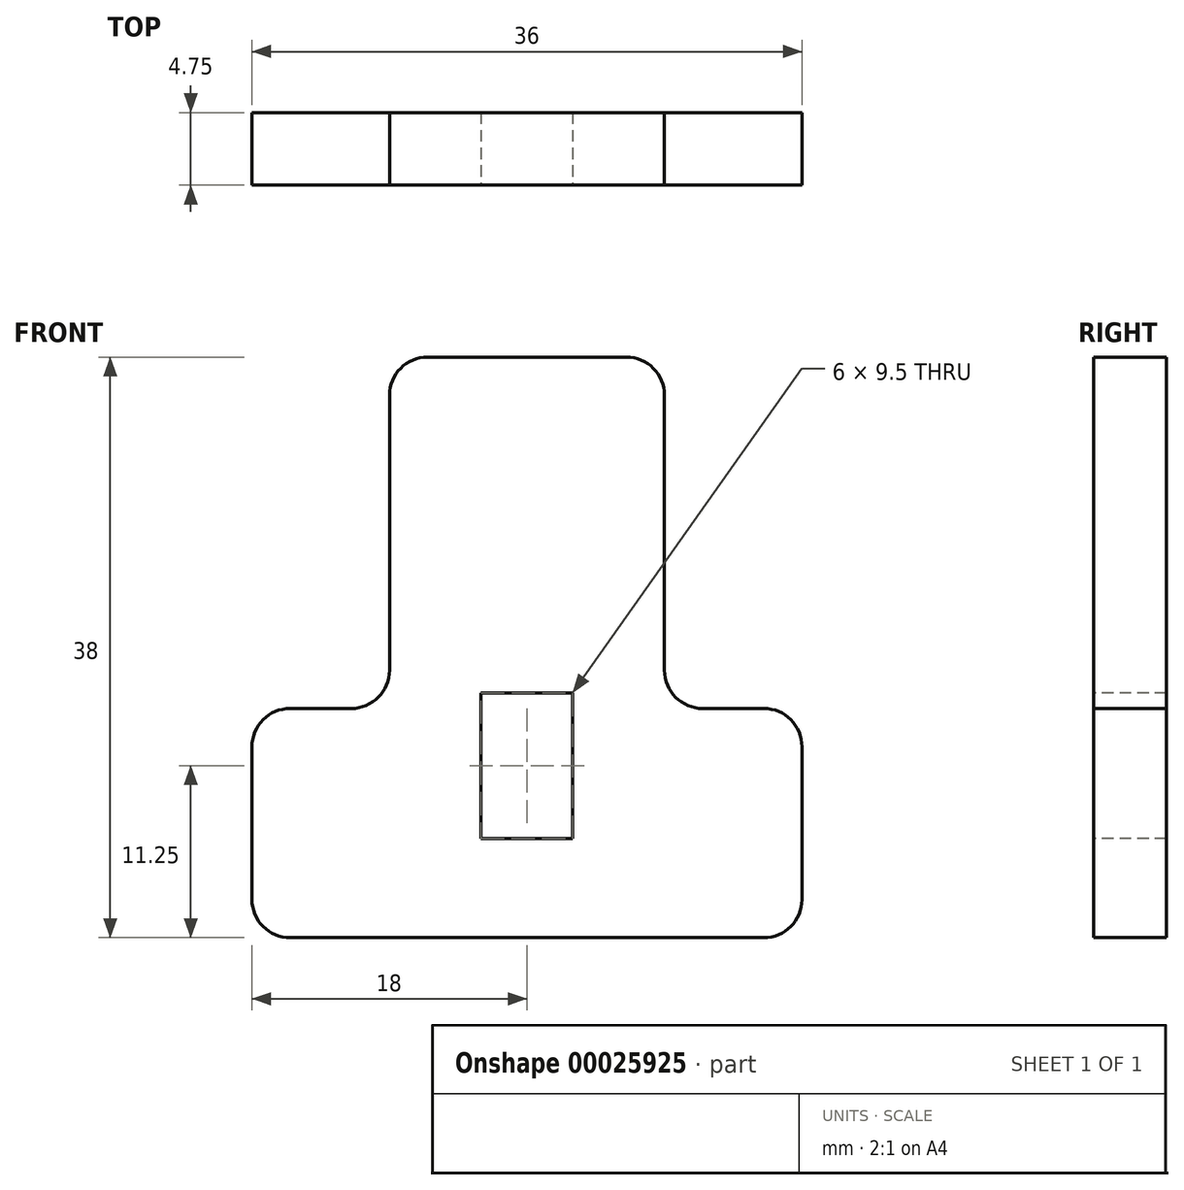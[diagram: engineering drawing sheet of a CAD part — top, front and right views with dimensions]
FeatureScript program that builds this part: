
annotation { "Feature Type Name" : "Feature", "Feature Type Description" : "" }
export const myFeature = defineFeature(function(context is Context, id is Id, definition is map)
    precondition{}
    {
        {
            var Q0;
            Q0=qCreatedBy(makeId("Front.planeOp"),FACE);
            var sketch = newSketch(context, id + "F0", { "sketchPlane" : qUnion([Q0])});
            skLineSegment(sketch, "E0", {"start": v(0, -15) * mm, "end": v(-18, -15) * mm});
            skLineSegment(sketch, "E1", {"start": v(-18, -15) * mm, "end": v(-18, 0) * mm});
            skLineSegment(sketch, "E2", {"start": v(-18, 0) * mm, "end": v(-9, 0) * mm});
            skLineSegment(sketch, "E3", {"start": v(-9, 0) * mm, "end": v(-9, 23) * mm});
            skLineSegment(sketch, "E4", {"start": v(-9, 23) * mm, "end": v(0, 23) * mm});
            skLineSegment(sketch, "E5.MirrorCS", {"start": v(9, 23) * mm, "end": v(0, 23) * mm});
            skLineSegment(sketch, "E6.MirrorCS", {"start": v(9, 0) * mm, "end": v(9, 23) * mm});
            skLineSegment(sketch, "E7.MirrorCS", {"start": v(18, 0) * mm, "end": v(9, 0) * mm});
            skLineSegment(sketch, "E8.MirrorCS", {"start": v(18, -15) * mm, "end": v(18, 0) * mm});
            skLineSegment(sketch, "E9.MirrorCS", {"start": v(0, -15) * mm, "end": v(18, -15) * mm});
            skLineSegment(sketch, "E10", {"start": v(0, 1) * mm, "end": v(-3, 1) * mm});
            skLineSegment(sketch, "E11", {"start": v(-3, 1) * mm, "end": v(-3, -8.5) * mm});
            skLineSegment(sketch, "E12", {"start": v(-3, -8.5) * mm, "end": v(0, -8.5) * mm});
            skLineSegment(sketch, "E13.MirrorCS", {"start": v(0, 1) * mm, "end": v(3, 1) * mm});
            skLineSegment(sketch, "E14.MirrorCS", {"start": v(3, 1) * mm, "end": v(3, -8.5) * mm});
            skLineSegment(sketch, "E15.MirrorCS", {"start": v(3, -8.5) * mm, "end": v(0, -8.5) * mm});
            skSolve(sketch);
        }
        {
            var Q0;
            Q0=makeQuery(id+"F0.imprint","IMPRINT",FACE,{"disambiguationData":[TD([[makeQuery(id+"F0.imprint","IMPRINT",EDGE,{"derivedFrom":sQuery(id+"F0.wireOp",EDGE,"E0")}),-1.0]])]});
            extrude(context, id + "F1", {"entities" : qUnion([Q0]), "oppositeDirection" : true, "depth" : 4.75 * mm});
        }
        {
            var Q0;
            Q0=makeQuery(id+"F1.opExtrude","SWEPT_EDGE",EDGE,{"disambiguationData":[OSD([sQuery(id+"F0.wireOp",EDGE,"E5.MirrorCS"),sQuery(id+"F0.wireOp",EDGE,"E6.MirrorCS")])]});
            var Q1;
            Q1=makeQuery(id+"F1.opExtrude","SWEPT_EDGE",EDGE,{"disambiguationData":[OSD([sQuery(id+"F0.wireOp",EDGE,"E6.MirrorCS"),sQuery(id+"F0.wireOp",EDGE,"E7.MirrorCS")])]});
            var Q2;
            Q2=makeQuery(id+"F1.opExtrude","SWEPT_EDGE",EDGE,{"disambiguationData":[OSD([sQuery(id+"F0.wireOp",EDGE,"E7.MirrorCS"),sQuery(id+"F0.wireOp",EDGE,"E8.MirrorCS")])]});
            var Q3;
            Q3=makeQuery(id+"F1.opExtrude","SWEPT_EDGE",EDGE,{"disambiguationData":[OSD([sQuery(id+"F0.wireOp",EDGE,"E8.MirrorCS"),sQuery(id+"F0.wireOp",EDGE,"E9.MirrorCS")])]});
            var Q4;
            Q4=makeQuery(id+"F1.opExtrude","SWEPT_EDGE",EDGE,{"disambiguationData":[OSD([sQuery(id+"F0.wireOp",EDGE,"E3"),sQuery(id+"F0.wireOp",EDGE,"E4")])]});
            var Q5;
            Q5=makeQuery(id+"F1.opExtrude","SWEPT_EDGE",EDGE,{"disambiguationData":[OSD([sQuery(id+"F0.wireOp",EDGE,"E1"),sQuery(id+"F0.wireOp",EDGE,"E2")])]});
            var Q6;
            Q6=makeQuery(id+"F1.opExtrude","SWEPT_EDGE",EDGE,{"disambiguationData":[OSD([sQuery(id+"F0.wireOp",EDGE,"E0"),sQuery(id+"F0.wireOp",EDGE,"E1")])]});
            var Q7;
            Q7=makeQuery(id+"F1.opExtrude","SWEPT_EDGE",EDGE,{"disambiguationData":[OSD([sQuery(id+"F0.wireOp",EDGE,"E2"),sQuery(id+"F0.wireOp",EDGE,"E3")])]});
            fillet(context, id + "F2", {"entities" : qUnion([Q0, Q1, Q2, Q3, Q4, Q5, Q6, Q7]), "radius" : 2.5 * mm, "tangentPropagation" : true, "allowEdgeOverflow" : false});
        }
    });
